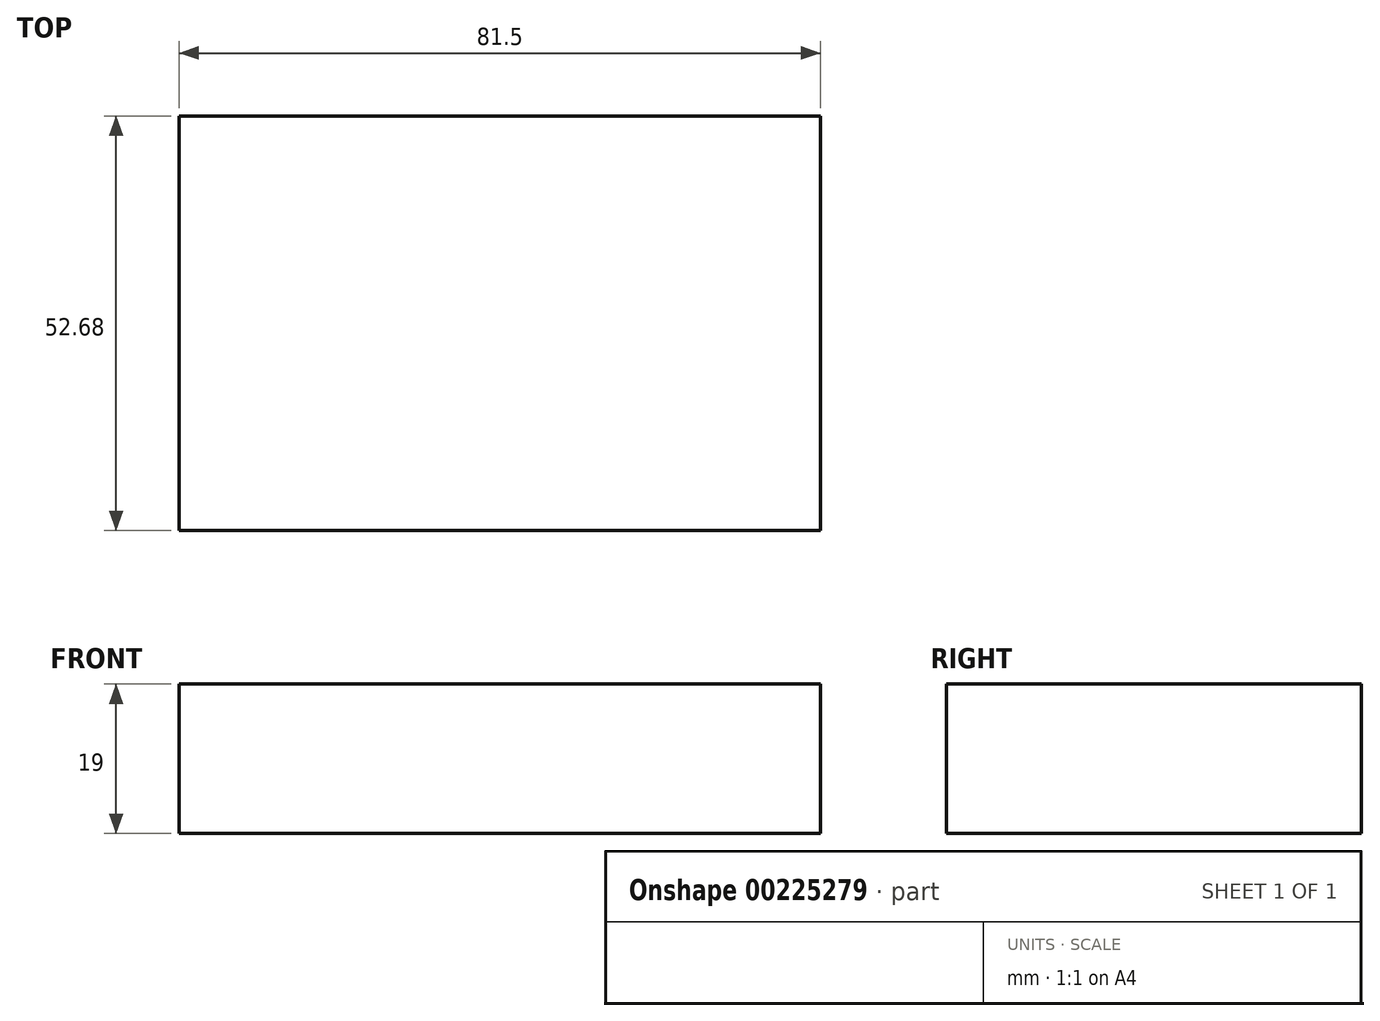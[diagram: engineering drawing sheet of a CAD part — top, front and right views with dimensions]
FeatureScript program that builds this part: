
annotation { "Feature Type Name" : "Feature", "Feature Type Description" : "" }
export const myFeature = defineFeature(function(context is Context, id is Id, definition is map)
    precondition{}
    {
        {
            var Q0;
            Q0=qCreatedBy(makeId("Top.planeOp"),FACE);
            var sketch = newSketch(context, id + "F0", { "sketchPlane" : qUnion([Q0])});
            skLineSegment(sketch, "E0.bottom", {"start": v(40.75, 26.34) * mm, "end": v(-40.75, 26.34) * mm});
            skLineSegment(sketch, "E0.top", {"start": v(40.75, -26.34) * mm, "end": v(-40.75, -26.34) * mm});
            skLineSegment(sketch, "E0.left", {"start": v(40.75, 26.34) * mm, "end": v(40.75, -26.34) * mm});
            skLineSegment(sketch, "E0.right", {"start": v(-40.75, 26.34) * mm, "end": v(-40.75, -26.34) * mm});
            skPoint(sketch, "E0.middle", {"position": v(0, 0) * mm});
            skSolve(sketch);
        }
        {
            var Q0;
            Q0 = qSketchRegion(id + "F0", true);
            extrude(context, id + "F1", {"entities" : qUnion([Q0]), "depth" : 19 * mm});
        }
    });
